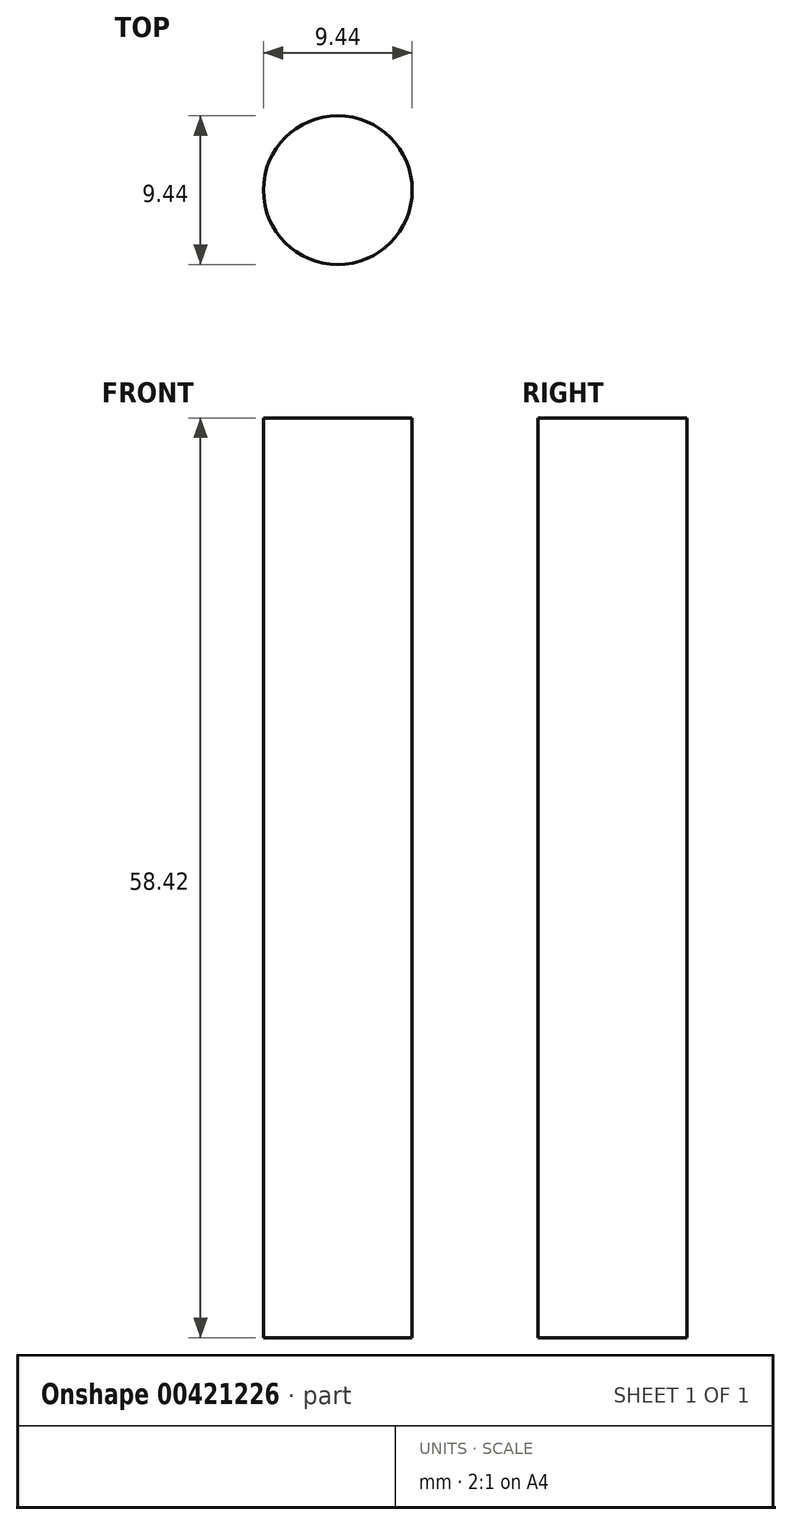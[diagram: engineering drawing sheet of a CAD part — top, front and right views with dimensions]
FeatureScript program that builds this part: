
annotation { "Feature Type Name" : "Feature", "Feature Type Description" : "" }
export const myFeature = defineFeature(function(context is Context, id is Id, definition is map)
    precondition{}
    {
        {
            var Q0;
            Q0=qCreatedBy(makeId("Top.planeOp"),FACE);
            var sketch = newSketch(context, id + "F0", { "sketchPlane" : qUnion([Q0])});
            skCircle(sketch, "E0", {"center": v(0, 0) * mm, "radius": 4.72 * mm});
            skSolve(sketch);
        }
        {
            var Q0;
            Q0 = qSketchRegion(id + "F0", true);
            extrude(context, id + "F1", {"entities" : qUnion([Q0]), "depth" : 58.42 * mm});
        }
    });
